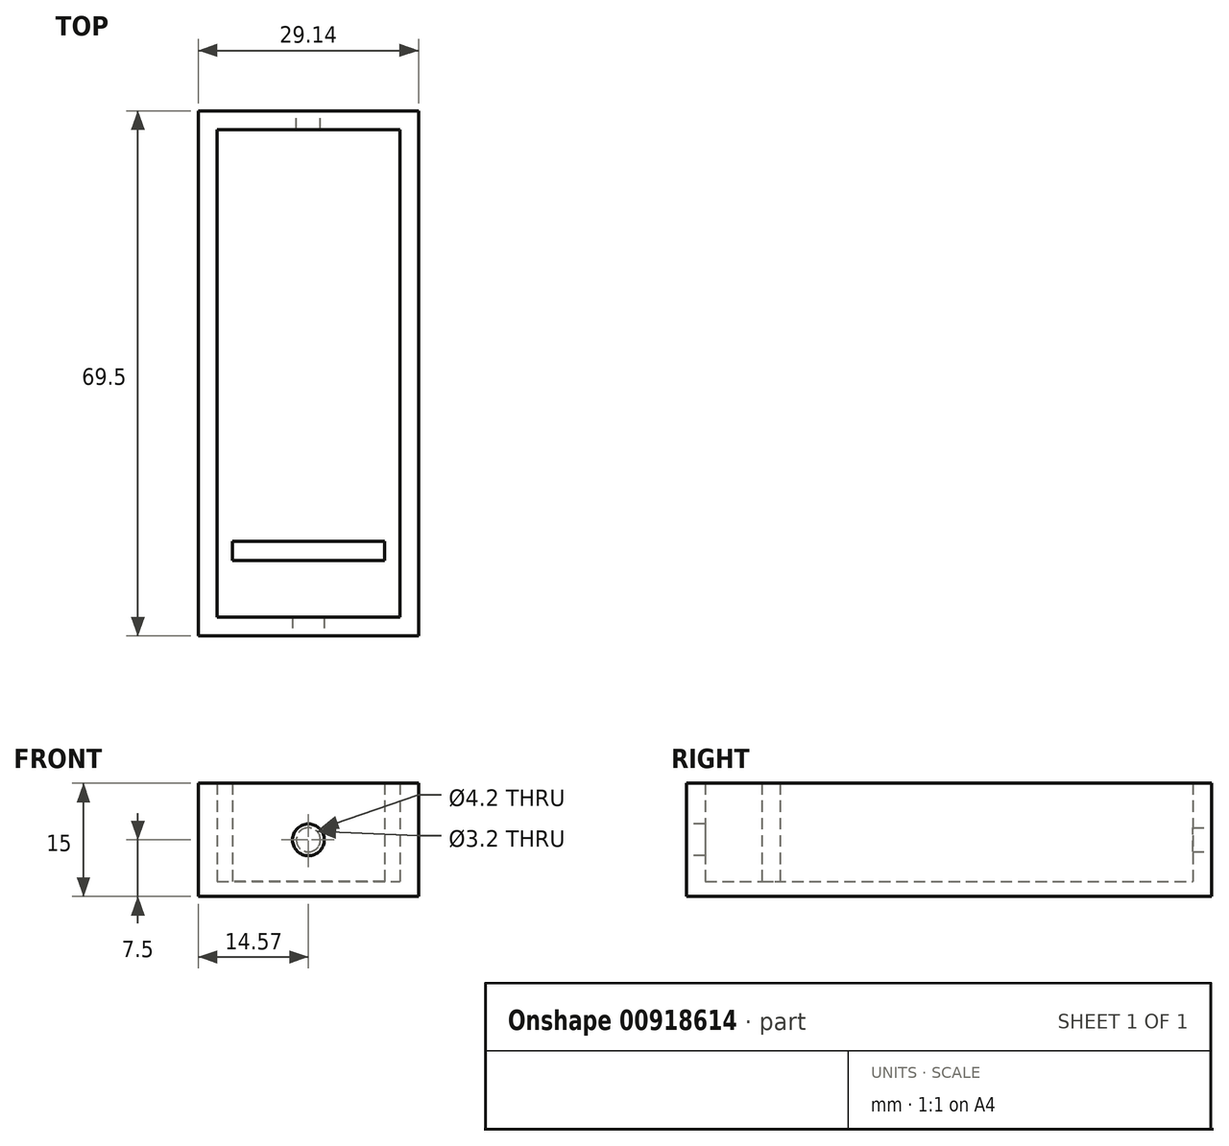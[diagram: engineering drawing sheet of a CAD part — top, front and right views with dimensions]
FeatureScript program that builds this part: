
annotation { "Feature Type Name" : "Feature", "Feature Type Description" : "" }
export const myFeature = defineFeature(function(context is Context, id is Id, definition is map)
    precondition{}
    {
        {
            var Q0;
            Q0=qCreatedBy(makeId("Top.planeOp"),FACE);
            var sketch = newSketch(context, id + "F0", { "sketchPlane" : qUnion([Q0])});
            skLineSegment(sketch, "E0.bottom", {"start": v(12.07, 27.25) * mm, "end": v(-12.08, 27.25) * mm});
            skLineSegment(sketch, "E0.top", {"start": v(12.07, -27.25) * mm, "end": v(-12.08, -27.25) * mm});
            skLineSegment(sketch, "E0.left", {"start": v(12.07, 27.25) * mm, "end": v(12.07, -27.25) * mm});
            skLineSegment(sketch, "E0.right", {"start": v(-12.08, 27.25) * mm, "end": v(-12.08, -27.25) * mm});
            skLineSegment(sketch, "E1.bottom", {"start": v(14.57, 29.75) * mm, "end": v(-14.57, 29.75) * mm});
            skLineSegment(sketch, "E1.top", {"start": v(14.57, -29.75) * mm, "end": v(-14.58, -29.75) * mm});
            skLineSegment(sketch, "E1.left", {"start": v(14.57, 29.75) * mm, "end": v(14.57, -29.75) * mm});
            skLineSegment(sketch, "E1.right", {"start": v(-14.57, 29.75) * mm, "end": v(-14.58, -29.75) * mm});
            skPoint(sketch, "E1.middle", {"position": v(0, 0) * mm});
            skSolve(sketch);
        }
        {
            var Q0;
            Q0=makeQuery(id+"F0.imprint","IMPRINT",FACE,{"disambiguationData":[TD([[makeQuery(id+"F0.imprint","IMPRINT",EDGE,{"derivedFrom":sQuery(id+"F0.wireOp",EDGE,"E0.bottom")}),1.0]])]});
            var Q1;
            Q1=makeQuery(id+"F0.imprint","IMPRINT",FACE,{"disambiguationData":[TD([[makeQuery(id+"F0.imprint","IMPRINT",EDGE,{"derivedFrom":sQuery(id+"F0.wireOp",EDGE,"E0.bottom")}),-1.0]])]});
            extrude(context, id + "F1", {"entities" : qUnion([Q0, Q1]), "depth" : 2 * mm, "offsetDistance" : 25 * mm});
        }
        {
            var Q0;
            Q0=makeQuery(id+"F0.imprint","IMPRINT",FACE,{"disambiguationData":[TD([[makeQuery(id+"F0.imprint","IMPRINT",EDGE,{"derivedFrom":sQuery(id+"F0.wireOp",EDGE,"E0.bottom")}),-1.0]])]});
            extrude(context, id + "F2", {"entities" : qUnion([Q0]), "operationType" : NewBodyOperationType.ADD, "depth" : 15 * mm, "offsetDistance" : 25 * mm});
        }
        {
            var Q0;
            Q0=makeQuery(id+"F2.opExtrude","SWEPT_FACE",FACE,{"disambiguationData":[OSD([sQuery(id+"F0.wireOp",EDGE,"E0.top")])]});
            var sketch = newSketch(context, id + "F3", { "sketchPlane" : qUnion([Q0])});
            skLineSegment(sketch, "E2.bottom", {"start": v(12.08, 2) * mm, "end": v(10.08, 2) * mm});
            skLineSegment(sketch, "E2.top", {"start": v(12.08, 15) * mm, "end": v(10.08, 15) * mm});
            skLineSegment(sketch, "E2.left", {"start": v(12.08, 2) * mm, "end": v(12.08, 15) * mm});
            skLineSegment(sketch, "E2.right", {"start": v(10.08, 2) * mm, "end": v(10.08, 15) * mm});
            skLineSegment(sketch, "E3.bottom", {"start": v(-12.07, 2) * mm, "end": v(-10.07, 2) * mm});
            skLineSegment(sketch, "E3.top", {"start": v(-12.07, 15) * mm, "end": v(-10.07, 15) * mm});
            skLineSegment(sketch, "E3.left", {"start": v(-12.07, 2) * mm, "end": v(-12.07, 15) * mm});
            skLineSegment(sketch, "E3.right", {"start": v(-10.07, 2) * mm, "end": v(-10.07, 15) * mm});
            skSolve(sketch);
        }
        {
            var Q0;
            Q0=makeQuery(id+"F3.imprint","IMPRINT",FACE,{"disambiguationData":[TD([[makeQuery(id+"F3.imprint","IMPRINT",EDGE,{"derivedFrom":sQuery(id+"F3.wireOp",EDGE,"E2.bottom")}),-1.0]])]});
            var Q1;
            Q1=makeQuery(id+"F3.imprint","IMPRINT",FACE,{"disambiguationData":[TD([[makeQuery(id+"F3.imprint","IMPRINT",EDGE,{"derivedFrom":sQuery(id+"F3.wireOp",EDGE,"E3.bottom")}),-1.0]])]});
            extrude(context, id + "F4", {"entities" : qUnion([Q0, Q1]), "operationType" : NewBodyOperationType.REMOVE, "oppositeDirection" : true, "depth" : 25 * mm, "offsetDistance" : 25 * mm});
        }
        {
            var Q0;
            Q0=makeQuery(id+"F1.opExtrude","CAP_FACE",FACE,{"disambiguationData":[OSD([sQuery(id+"F0.wireOp",EDGE,"E1.bottom"),sQuery(id+"F0.wireOp",EDGE,"E1.top"),sQuery(id+"F0.wireOp",EDGE,"E1.left"),sQuery(id+"F0.wireOp",EDGE,"E1.right")])],"isStart":true});
            var sketch = newSketch(context, id + "F5", { "sketchPlane" : qUnion([Q0])});
            skLineSegment(sketch, "E4.bottom", {"start": v(-14.58, 29.75) * mm, "end": v(14.57, 29.75) * mm});
            skLineSegment(sketch, "E4.top", {"start": v(-14.58, 39.75) * mm, "end": v(14.57, 39.75) * mm});
            skLineSegment(sketch, "E4.left", {"start": v(-14.58, 29.75) * mm, "end": v(-14.58, 39.75) * mm});
            skLineSegment(sketch, "E4.right", {"start": v(14.57, 29.75) * mm, "end": v(14.57, 39.75) * mm});
            skLineSegment(sketch, "E5.bottom", {"start": v(-12.08, 29.75) * mm, "end": v(12.07, 29.75) * mm});
            skLineSegment(sketch, "E5.top", {"start": v(-12.08, 37.25) * mm, "end": v(12.07, 37.25) * mm});
            skLineSegment(sketch, "E5.left", {"start": v(-12.08, 29.75) * mm, "end": v(-12.08, 37.25) * mm});
            skLineSegment(sketch, "E5.right", {"start": v(12.07, 29.75) * mm, "end": v(12.07, 37.25) * mm});
            skSolve(sketch);
        }
        {
            var Q0;
            Q0=makeQuery(id+"F5.imprint","IMPRINT",FACE,{"disambiguationData":[TD([[makeQuery(id+"F5.imprint","IMPRINT",EDGE,{"derivedFrom":sQuery(id+"F5.wireOp",EDGE,"E4.top")}),-1.0]])]});
            extrude(context, id + "F6", {"entities" : qUnion([Q0]), "operationType" : NewBodyOperationType.ADD, "oppositeDirection" : true, "depth" : 15 * mm, "offsetDistance" : 25 * mm});
        }
        {
            var Q0;
            Q0=makeQuery(id+"F5.imprint","IMPRINT",FACE,{"disambiguationData":[TD([[makeQuery(id+"F5.imprint","IMPRINT",EDGE,{"derivedFrom":sQuery(id+"F5.wireOp",EDGE,"E5.top")}),-1.0]])]});
            extrude(context, id + "F7", {"entities" : qUnion([Q0]), "operationType" : NewBodyOperationType.ADD, "oppositeDirection" : true, "depth" : 2 * mm, "offsetDistance" : 25 * mm});
        }
        {
            var Q0;
            Q0=makeQuery(id+"F6.opExtrude","SWEPT_FACE",FACE,{"disambiguationData":[OSD([sQuery(id+"F5.wireOp",EDGE,"E4.top")])]});
            var sketch = newSketch(context, id + "F8", { "sketchPlane" : qUnion([Q0])});
            skCircle(sketch, "E6", {"center": v(0, 7.5) * mm, "radius": 2.1 * mm});
            skPoint(sketch, "E6.centerSnap0", {"position": v(14.57, 7.5) * mm});
            skPoint(sketch, "E6.centerSnap1", {"position": v(0, 15) * mm});
            skSolve(sketch);
        }
        {
            var Q0;
            Q0=makeQuery(id+"F8.imprint","IMPRINT",FACE,{"disambiguationData":[TD([[makeQuery(id+"F8.imprint","IMPRINT",EDGE,{"derivedFrom":sQuery(id+"F8.wireOp",EDGE,"E6")}),1.0]])]});
            extrude(context, id + "F9", {"entities" : qUnion([Q0]), "operationType" : NewBodyOperationType.REMOVE, "oppositeDirection" : true, "depth" : 5 * mm, "offsetDistance" : 25 * mm});
        }
        {
            var Q0;
            {var subQ0=sQuery(id+"F0.wireOp",EDGE,"E1.bottom");Q0=makeQuery(id+"F2.boolean.opBoolean","MERGE",FACE,{"derivedFrom":[makeQuery(id+"F1.opExtrude","SWEPT_FACE",FACE,{"disambiguationData":[OSD([subQ0])]}),makeQuery(id+"F2.opExtrude","SWEPT_FACE",FACE,{"disambiguationData":[OSD([subQ0])]})]});}
            var sketch = newSketch(context, id + "F10", { "sketchPlane" : qUnion([Q0])});
            skCircle(sketch, "E7", {"center": v(0, 7.5) * mm, "radius": 1.6 * mm});
            skPoint(sketch, "E7.centerSnap0", {"position": v(0, 15) * mm});
            skPoint(sketch, "E7.centerSnap1", {"position": v(-14.57, 7.5) * mm});
            skSolve(sketch);
        }
        {
            var Q0;
            Q0 = qSketchRegion(id + "F10", true);
            extrude(context, id + "F11", {"entities" : qUnion([Q0]), "operationType" : NewBodyOperationType.REMOVE, "oppositeDirection" : true, "depth" : 25 * mm, "offsetDistance" : 25 * mm});
        }
    });
